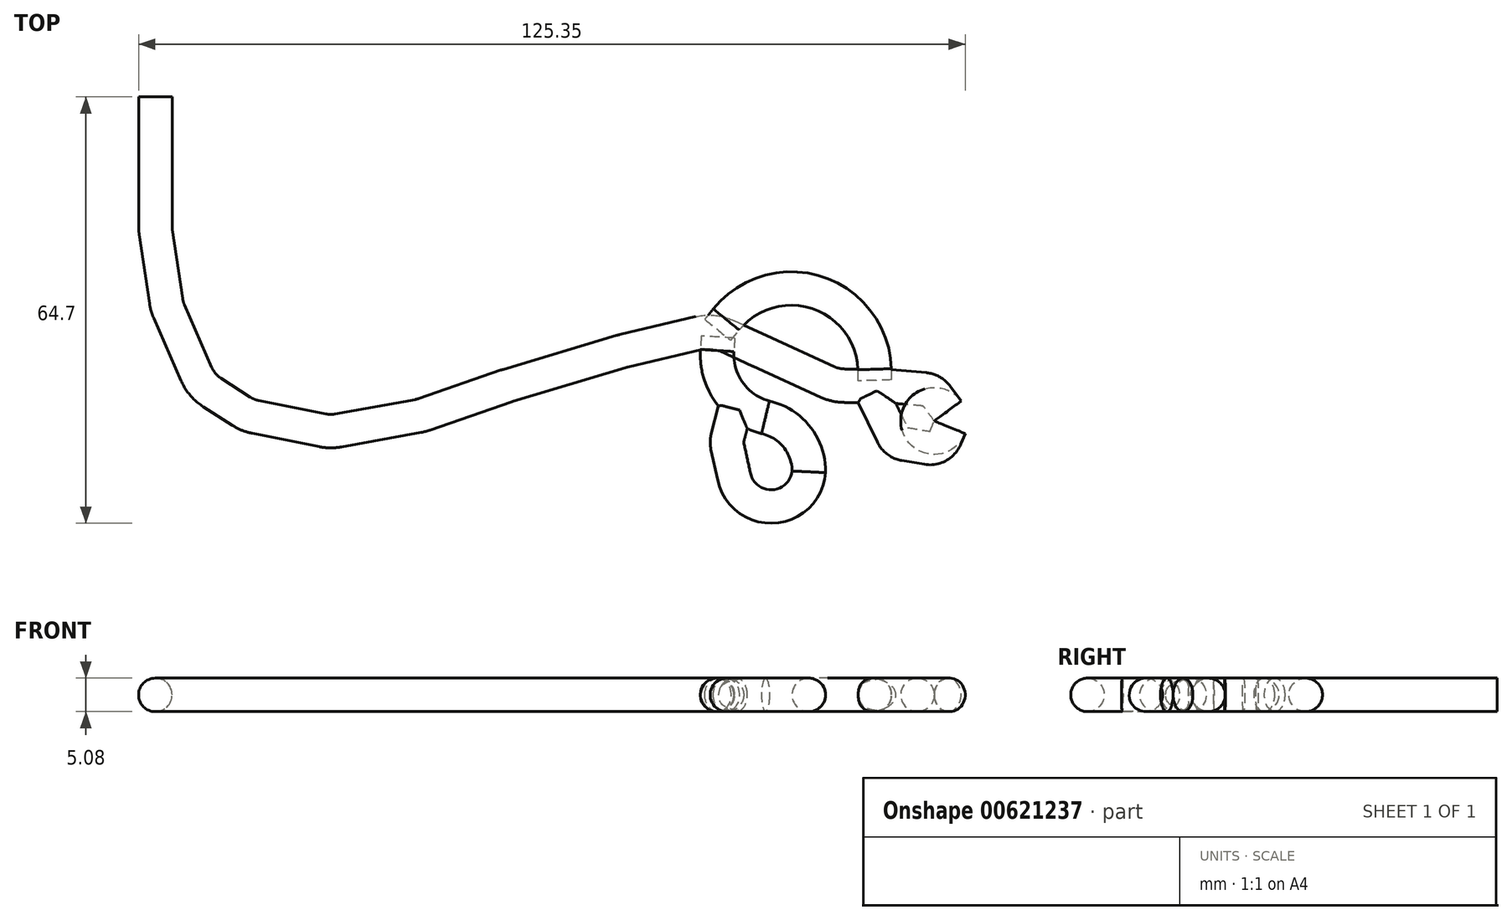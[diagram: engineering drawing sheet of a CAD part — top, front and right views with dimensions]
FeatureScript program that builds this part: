
annotation { "Feature Type Name" : "Feature", "Feature Type Description" : "" }
export const myFeature = defineFeature(function(context is Context, id is Id, definition is map)
    precondition{}
    {
        {
            var Q0;
            Q0=qCreatedBy(makeId("Top.planeOp"),FACE);
            var sketch = newSketch(context, id + "F0", { "sketchPlane" : qUnion([Q0])});
            skLineSegment(sketch, "E0", {"start": v(-53.34, 31.8) * mm, "end": v(-53.34, 22.04) * mm});
            skLineSegment(sketch, "E1", {"start": v(-53.34, 22.04) * mm, "end": v(-53.34, 12.24) * mm});
            skLineSegment(sketch, "E2", {"start": v(-53.27, 11.3) * mm, "end": v(-51.71, 0.84) * mm});
            skLineSegment(sketch, "E3", {"start": v(-51.25, -0.77) * mm, "end": v(-47.1, -10.26) * mm});
            skLineSegment(sketch, "E4", {"start": v(-44.71, -13.06) * mm, "end": v(-40.33, -15.88) * mm});
            skLineSegment(sketch, "E5", {"start": v(-38.14, -16.76) * mm, "end": v(-27.98, -18.8) * mm});
            skLineSegment(sketch, "E6", {"start": v(-25.6, -18.82) * mm, "end": v(-13.5, -16.62) * mm});
            skLineSegment(sketch, "E7", {"start": v(-12.56, -16.37) * mm, "end": v(-0.13, -12.06) * mm});
            skLineSegment(sketch, "E8", {"start": v(0.13, -11.98) * mm, "end": v(17.35, -6.82) * mm});
            skLineSegment(sketch, "E9", {"start": v(17.71, -6.72) * mm, "end": v(29.16, -4.01) * mm});
            skLineSegment(sketch, "E10", {"start": v(33.3, -4.43) * mm, "end": v(38.3, -6.75) * mm});
            skLineSegment(sketch, "E11", {"start": v(38.33, -6.77) * mm, "end": v(48.58, -11.45) * mm});
            skLineSegment(sketch, "E12", {"start": v(51.21, -12.02) * mm, "end": v(57.23, -12.02) * mm});
            skPoint(sketch, "E13.visualSharp", {"position": v(49.83, -12.02) * mm});
            skArc(sketch, "E13.filletArc", {"start": v(48.58, -11.45) * mm, "mid": v(49.87, -11.88) * mm, "end": v(51.21, -12.02) * mm});
            skPoint(sketch, "E14.visualSharp", {"position": v(38.31, -6.76) * mm});
            skArc(sketch, "E14.filletArc", {"start": v(38.3, -6.75) * mm, "mid": v(38.31, -6.76) * mm, "end": v(38.33, -6.77) * mm});
            skPoint(sketch, "E15.visualSharp", {"position": v(31.3, -3.5) * mm});
            skArc(sketch, "E15.filletArc", {"start": v(33.3, -4.43) * mm, "mid": v(31.27, -3.87) * mm, "end": v(29.16, -4.01) * mm});
            skPoint(sketch, "E16.visualSharp", {"position": v(17.53, -6.76) * mm});
            skArc(sketch, "E16.filletArc", {"start": v(17.71, -6.72) * mm, "mid": v(17.53, -6.76) * mm, "end": v(17.35, -6.82) * mm});
            skPoint(sketch, "E17.visualSharp", {"position": v(0, -12.02) * mm});
            skArc(sketch, "E17.filletArc", {"start": v(0.13, -11.98) * mm, "mid": v(0, -12.02) * mm, "end": v(-0.13, -12.06) * mm});
            skPoint(sketch, "E18.visualSharp", {"position": v(-13.02, -16.53) * mm});
            skArc(sketch, "E18.filletArc", {"start": v(-13.5, -16.62) * mm, "mid": v(-13.03, -16.5) * mm, "end": v(-12.56, -16.37) * mm});
            skPoint(sketch, "E19.visualSharp", {"position": v(-26.8, -19.03) * mm});
            skArc(sketch, "E19.filletArc", {"start": v(-27.98, -18.8) * mm, "mid": v(-26.8, -18.92) * mm, "end": v(-25.6, -18.82) * mm});
            skPoint(sketch, "E20.visualSharp", {"position": v(-39.32, -16.53) * mm});
            skArc(sketch, "E20.filletArc", {"start": v(-40.33, -15.88) * mm, "mid": v(-39.27, -16.42) * mm, "end": v(-38.14, -16.76) * mm});
            skPoint(sketch, "E21.visualSharp", {"position": v(-46.33, -12.02) * mm});
            skArc(sketch, "E21.filletArc", {"start": v(-47.1, -10.26) * mm, "mid": v(-46.11, -11.84) * mm, "end": v(-44.71, -13.06) * mm});
            skPoint(sketch, "E22.visualSharp", {"position": v(-51.59, 0) * mm});
            skArc(sketch, "E22.filletArc", {"start": v(-51.71, 0.84) * mm, "mid": v(-51.53, 0.02) * mm, "end": v(-51.25, -0.77) * mm});
            skPoint(sketch, "E23.visualSharp", {"position": v(-53.34, 11.77) * mm});
            skArc(sketch, "E23.filletArc", {"start": v(-53.34, 12.24) * mm, "mid": v(-53.32, 11.77) * mm, "end": v(-53.27, 11.3) * mm});
            skLineSegment(sketch, "E24", {"start": v(57.46, -12.03) * mm, "end": v(63.33, -12.57) * mm});
            skLineSegment(sketch, "E25", {"start": v(65.14, -13.6) * mm, "end": v(66.81, -15.86) * mm});
            skLineSegment(sketch, "E26", {"start": v(67.12, -18.33) * mm, "end": v(66.47, -19.9) * mm});
            skLineSegment(sketch, "E27", {"start": v(63.7, -21.45) * mm, "end": v(60.3, -20.88) * mm});
            skLineSegment(sketch, "E28", {"start": v(58.43, -19.47) * mm, "end": v(55.37, -13.13) * mm});
            skPoint(sketch, "E29.visualSharp", {"position": v(57.35, -12.02) * mm});
            skArc(sketch, "E29.filletArc", {"start": v(57.46, -12.03) * mm, "mid": v(57.35, -12.02) * mm, "end": v(57.23, -12.02) * mm});
            skPoint(sketch, "E30.visualSharp", {"position": v(64.47, -12.67) * mm});
            skArc(sketch, "E30.filletArc", {"start": v(65.14, -13.6) * mm, "mid": v(64.35, -12.88) * mm, "end": v(63.33, -12.57) * mm});
            skPoint(sketch, "E31.visualSharp", {"position": v(67.65, -17) * mm});
            skArc(sketch, "E31.filletArc", {"start": v(67.12, -18.33) * mm, "mid": v(67.29, -17.05) * mm, "end": v(66.81, -15.86) * mm});
            skPoint(sketch, "E32.visualSharp", {"position": v(65.7, -21.8) * mm});
            skArc(sketch, "E32.filletArc", {"start": v(63.7, -21.45) * mm, "mid": v(65.36, -21.17) * mm, "end": v(66.47, -19.9) * mm});
            skPoint(sketch, "E33.visualSharp", {"position": v(59, -20.66) * mm});
            skArc(sketch, "E33.filletArc", {"start": v(58.43, -19.47) * mm, "mid": v(59.2, -20.4) * mm, "end": v(60.3, -20.88) * mm});
            skSolve(sketch);
        }
        {
            var Q0;
            Q0=sQuery(id+"F0.wireOp",VERTEX,"E12.end");
            var Q1;
            Q1=sQuery(id+"F0.wireOp",EDGE,"E12");
            cPlane(context, id + "F1", {"entities" : qUnion([Q0, Q1]), "cplaneType" : CPlaneType.LINE_POINT, "offset" : 25.4 * mm, "width" : 152.4 * mm, "height" : 152.4 * mm});
        }
        {
            var Q0;
            Q0=qCreatedBy(id+"F1.planeOp",FACE);
            var sketch = newSketch(context, id + "F2", { "sketchPlane" : qUnion([Q0])});
            skCircle(sketch, "E34", {"center": v(-12.02, 0) * mm, "radius": 2.54 * mm});
            skSolve(sketch);
        }
        {
            var Q0;
            Q0 = qSketchRegion(id + "F2", true);
            var Q1;
            Q1 = qConstructionFilter(qBodyType(qCreatedBy(id + "F0" ,EDGE), BodyType.WIRE), ConstructionObject.NO);
            sweep(context, id + "F3", {"profiles" : qUnion([Q0]), "path" : qUnion([Q1])});
        }
        {
            var Q0;
            Q0=qCreatedBy(makeId("Top.planeOp"),FACE);
            var sketch = newSketch(context, id + "F4", { "sketchPlane" : qUnion([Q0])});
            skArc(sketch, "E35", {"start": v(34.42, -25.84) * mm, "mid": v(40.41, -30.35) * mm, "end": v(45.75, -25.09) * mm});
            skArc(sketch, "E36", {"start": v(45.75, -25.09) * mm, "mid": v(43.94, -19.79) * mm, "end": v(39.18, -16.83) * mm});
            skArc(sketch, "E37", {"start": v(31.86, -6.68) * mm, "mid": v(33.7, -13.07) * mm, "end": v(39.18, -16.83) * mm});
            skLineSegment(sketch, "E38", {"start": v(34.42, -25.84) * mm, "end": v(33.4, -21.14) * mm});
            skLineSegment(sketch, "E39", {"start": v(33.42, -19.96) * mm, "end": v(34.57, -15.55) * mm});
            skPoint(sketch, "E40.visualSharp", {"position": v(33.27, -20.55) * mm});
            skArc(sketch, "E40.filletArc", {"start": v(33.42, -19.96) * mm, "mid": v(33.34, -20.55) * mm, "end": v(33.4, -21.14) * mm});
            skSolve(sketch);
        }
        {
            var Q0;
            Q0=sQuery(id+"F4.wireOp",VERTEX,"E39.end");
            var Q1;
            Q1=sQuery(id+"F4.wireOp",EDGE,"E39");
            cPlane(context, id + "F5", {"entities" : qUnion([Q0, Q1]), "cplaneType" : CPlaneType.LINE_POINT, "offset" : 25.4 * mm, "width" : 152.4 * mm, "height" : 152.4 * mm});
        }
        {
            var Q0;
            Q0=qCreatedBy(id+"F5.planeOp",FACE);
            var sketch = newSketch(context, id + "F6", { "sketchPlane" : qUnion([Q0])});
            skCircle(sketch, "E41", {"center": v(-37.37, 0) * mm, "radius": 2.54 * mm});
            skSolve(sketch);
        }
        {
            var Q0;
            Q0 = qSketchRegion(id + "F6", true);
            var Q1;
            Q1 = qConstructionFilter(qBodyType(qCreatedBy(id + "F4" ,EDGE), BodyType.WIRE), ConstructionObject.NO);
            sweep(context, id + "F7", {"profiles" : qUnion([Q0]), "path" : qUnion([Q1])});
        }
        {
            var Q0;
            Q0=makeQuery(id+"F7.opSweep","CAP_FACE",FACE,{"disambiguationData":[OSD([sQuery(id+"F4.wireOp",VERTEX,"E37.start"),sQuery(id+"F6.wireOp",EDGE,"E41")])],"isStart":false});
            extrude(context, id + "F8", {"entities" : qUnion([Q0]), "depth" : 2.06 * mm, "offsetDistance" : 25.4 * mm});
        }
        {
            var Q0;
            Q0=qCreatedBy(makeId("Top.planeOp"),FACE);
            var sketch = newSketch(context, id + "F9", { "sketchPlane" : qUnion([Q0])});
            skArc(sketch, "E42", {"start": v(55.74, -9.53) * mm, "mid": v(47.12, 2.08) * mm, "end": v(33.24, -1.97) * mm});
            skLineSegment(sketch, "E43", {"start": v(33.24, -1.97) * mm, "end": v(42.34, 9.3) * mm, "construction": true});
            skSolve(sketch);
        }
        {
            var Q0;
            Q0=sQuery(id+"F9.wireOp",EDGE,"E43");
            var Q1;
            Q1=sQuery(id+"F9.wireOp",VERTEX,"E42.end");
            cPlane(context, id + "F10", {"entities" : qUnion([Q0, Q1]), "cplaneType" : CPlaneType.LINE_POINT, "offset" : 25.4 * mm, "width" : 152.4 * mm, "height" : 152.4 * mm});
        }
        {
            var Q0;
            Q0=qCreatedBy(id+"F10.planeOp",FACE);
            var sketch = newSketch(context, id + "F11", { "sketchPlane" : qUnion([Q0])});
            skCircle(sketch, "E44", {"center": v(-27.1, 0) * mm, "radius": 2.54 * mm});
            skSolve(sketch);
        }
        {
            var Q0;
            Q0 = qSketchRegion(id + "F11", true);
            var Q1;
            Q1=sQuery(id+"F9.wireOp",EDGE,"E42");
            sweep(context, id + "F12", {"profiles" : qUnion([Q0]), "path" : qUnion([Q1])});
        }
        {
            var Q0;
            Q0=makeQuery(id+"F12.opSweep","CAP_FACE",FACE,{"disambiguationData":[OSD([sQuery(id+"F9.wireOp",VERTEX,"E42.start"),sQuery(id+"F11.wireOp",EDGE,"E44")])],"isStart":false});
            extrude(context, id + "F13", {"entities" : qUnion([Q0]), "depth" : 1.68 * mm, "offsetDistance" : 25.4 * mm});
        }
        {
            var Q0;
            Q0=makeQuery(id+"F12.opSweep","CAP_FACE",FACE,{"disambiguationData":[OSD([sQuery(id+"F9.wireOp",VERTEX,"E42.end"),sQuery(id+"F11.wireOp",EDGE,"E44")])],"isStart":true});
            extrude(context, id + "F14", {"entities" : qUnion([Q0]), "depth" : 2.03 * mm, "offsetDistance" : 25.4 * mm});
        }
    });
